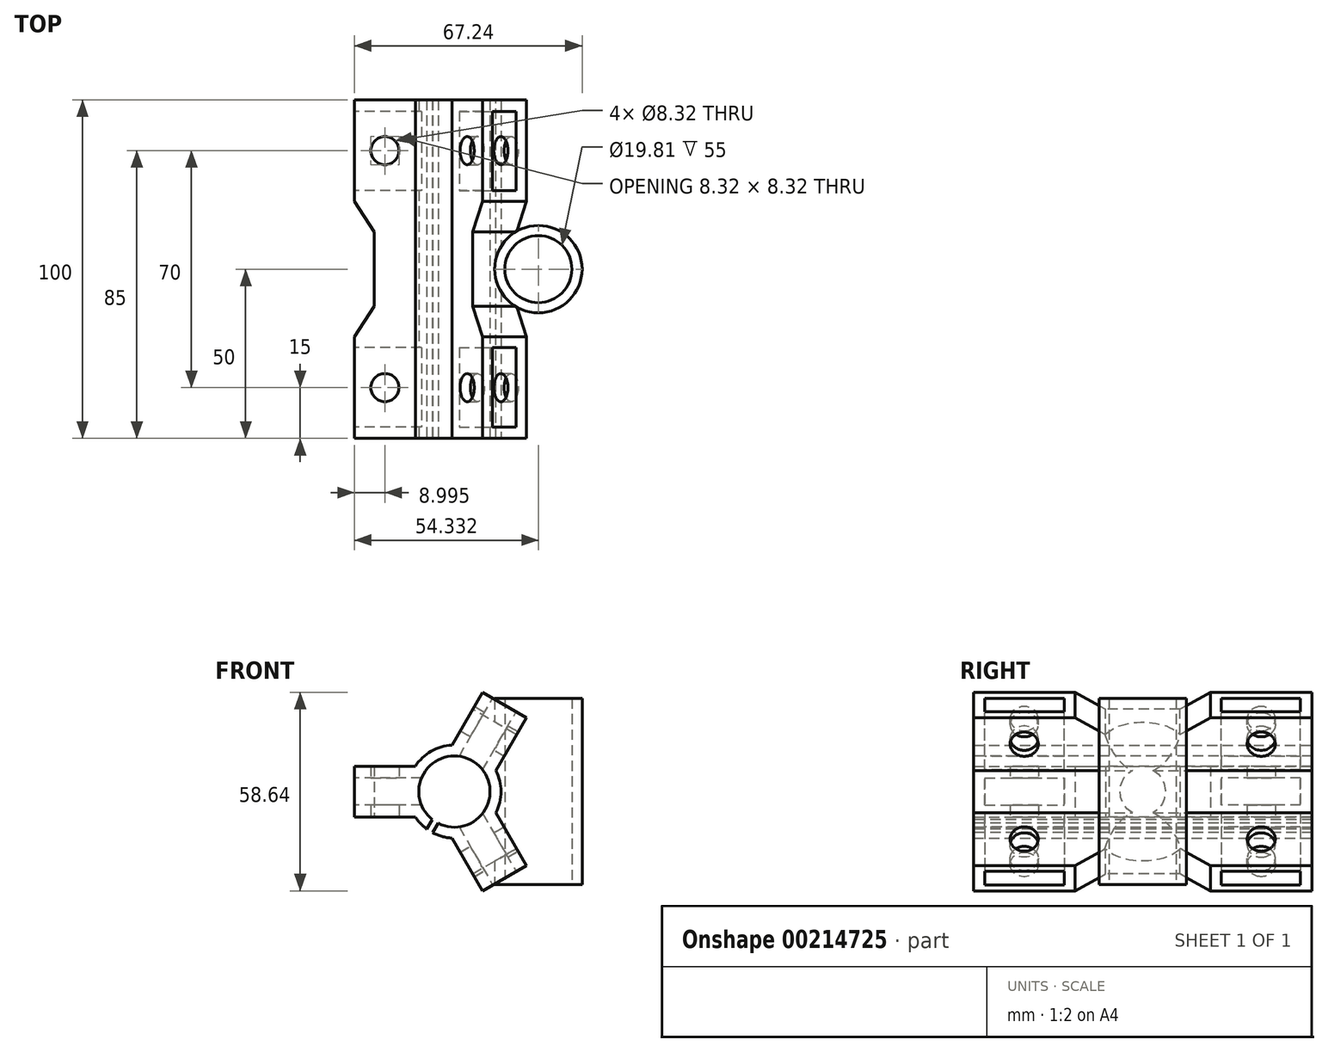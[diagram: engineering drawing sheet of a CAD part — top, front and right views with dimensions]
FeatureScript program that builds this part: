
annotation { "Feature Type Name" : "Feature", "Feature Type Description" : "" }
export const myFeature = defineFeature(function(context is Context, id is Id, definition is map)
    precondition{}
    {
        {
            var Q0;
            Q0=qCreatedBy(makeId("Top.planeOp"),FACE);
            var sketch = newSketch(context, id + "F0", { "sketchPlane" : qUnion([Q0])});
            skLineSegment(sketch, "E0", {"start": v(0, 0) * mm, "end": v(-9.53, 0) * mm, "construction": true});
            skLineSegment(sketch, "E1", {"start": v(-9.53, 0) * mm, "end": v(-9.53, 50) * mm, "construction": true});
            skLineSegment(sketch, "E2", {"start": v(-11.52, 0) * mm, "end": v(-11.53, 50) * mm});
            skLineSegment(sketch, "E3", {"start": v(-11.52, 0) * mm, "end": v(-29.52, 0) * mm});
            skLineSegment(sketch, "E4", {"start": v(-29.52, 0) * mm, "end": v(-29.53, 30) * mm});
            skCircle(sketch, "E5", {"center": v(-20.53, 15) * mm, "radius": 11 * mm, "construction": true});
            skCircle(sketch, "E6", {"center": v(-20.53, 15) * mm, "radius": 4.16 * mm});
            skLineSegment(sketch, "E7", {"start": v(-11.53, 39) * mm, "end": v(-23.75, 39) * mm, "construction": true});
            skLineSegment(sketch, "E8", {"start": v(-29.53, 30) * mm, "end": v(-23.75, 39) * mm});
            skLineSegment(sketch, "E9", {"start": v(-23.75, 39) * mm, "end": v(-23.75, 50) * mm});
            skLineSegment(sketch, "E10", {"start": v(-11.53, 50) * mm, "end": v(-23.75, 50) * mm, "construction": true});
            skLineSegment(sketch, "E11.MirrorCS", {"start": v(-23.75, 61) * mm, "end": v(-23.75, 50) * mm});
            skLineSegment(sketch, "E12.MirrorCS", {"start": v(-29.52, 70) * mm, "end": v(-23.75, 61) * mm});
            skLineSegment(sketch, "E13.MirrorCS", {"start": v(-29.53, 100) * mm, "end": v(-29.53, 70) * mm});
            skLineSegment(sketch, "E14.MirrorCS", {"start": v(-11.52, 100) * mm, "end": v(-29.52, 100) * mm});
            skLineSegment(sketch, "E15.MirrorCS", {"start": v(-11.53, 100) * mm, "end": v(-11.53, 50) * mm});
            skCircle(sketch, "E16.MirrorC", {"center": v(-20.53, 85) * mm, "radius": 4.16 * mm});
            skLineSegment(sketch, "E17.MirrorCS", {"start": v(-9.53, 100) * mm, "end": v(-9.53, 50) * mm, "construction": true});
            skCircle(sketch, "E18.MirrorC", {"center": v(-20.53, 85) * mm, "radius": 11 * mm, "construction": true});
            skSolve(sketch);
        }
        {
            var Q0;
            Q0=makeQuery(id+"F0.imprint","IMPRINT",FACE,{"disambiguationData":[TD([[makeQuery(id+"F0.imprint","IMPRINT",EDGE,{"derivedFrom":sQuery(id+"F0.wireOp",EDGE,"E2")}),1.0]])]});
            extrude(context, id + "F1", {"entities" : qUnion([Q0]), "depth" : 15 * mm});
        }
        {
            var Q0;
            Q0=makeQuery(id+"F1.opExtrude","SWEPT_FACE",FACE,{"disambiguationData":[OSD([sQuery(id+"F0.wireOp",EDGE,"E3")])]});
            var sketch = newSketch(context, id + "F2", { "sketchPlane" : qUnion([Q0])});
            skCircle(sketch, "E19", {"center": v(0, 7.5) * mm, "radius": 13.75 * mm, "construction": true});
            skCircle(sketch, "E20", {"center": v(0, 7.5) * mm, "radius": 10.53 * mm, "construction": true});
            skPoint(sketch, "E21.endSnap0", {"position": v(-11.52, 7.5) * mm});
            skArc(sketch, "E22", {"start": v(-6.88, 19.4) * mm, "mid": v(-13.75, 7.5) * mm, "end": v(-6.88, -4.4) * mm});
            skLineSegment(sketch, "E23", {"start": v(0, 7.5) * mm, "end": v(-10.53, 7.5) * mm, "construction": true});
            skLineSegment(sketch, "E24", {"start": v(0, 7.5) * mm, "end": v(-5.26, -1.61) * mm, "construction": true});
            skLineSegment(sketch, "E25", {"start": v(0, 7.5) * mm, "end": v(-5.26, 16.61) * mm, "construction": true});
            skArc(sketch, "E26", {"start": v(-5.26, 16.61) * mm, "mid": v(-10.53, 7.5) * mm, "end": v(-5.26, -1.61) * mm});
            skLineSegment(sketch, "E27", {"start": v(-5.26, 16.61) * mm, "end": v(-6.88, 19.4) * mm});
            skLineSegment(sketch, "E28", {"start": v(-5.26, -1.61) * mm, "end": v(-6.88, -4.4) * mm});
            skCircle(sketch, "E29", {"center": v(0, 7.5) * mm, "radius": 9.53 * mm, "construction": true});
            skSolve(sketch);
        }
        {
            var Q0;
            {var subQ0=sQuery(id+"F2.wireOp",EDGE,"E19");var subQ1=sQuery(id+"F0.wireOp",EDGE,"E3");var subQ2=makeQuery(id+"F1.opExtrude","SWEPT_EDGE",EDGE,{"disambiguationData":[OSD([sQuery(id+"F0.wireOp",EDGE,"E2"),subQ1])]});var subQ3=makeQuery(id+"F2.imprint","INTERSECT",VERTEX,{"derivedFrom":[subQ2,makeQuery(id+"F1.opExtrude","CAP_EDGE",EDGE,{"disambiguationData":[OSD([subQ1])],"isStart":true}),subQ0]});Q0=makeQuery(id+"F2.imprint","IMPRINT",FACE,{"disambiguationData":[TD([[makeQuery(id+"F2.imprint","IMPRINT",EDGE,{"disambiguationData":[TD([[subQ3,1.0]])],"derivedFrom":subQ0}),1.0]])]});}
            var Q1;
            {var subQ0=sQuery(id+"F2.wireOp",EDGE,"g3xJxAlq-R5pZ-Eeo2-CjEf-WmfwMOpCXLWw");Q1=makeQuery(id+"F2.imprint","IMPRINT",FACE,{"disambiguationData":[TD([[makeQuery(id+"F2.imprint","IMPRINT",EDGE,{"derivedFrom":subQ0}),-1.0]])]});}
            var Q2;
            Q2=makeQuery(id+"F2.imprint","IMPRINT",FACE,{"disambiguationData":[TD([[makeQuery(id+"F2.imprint","IMPRINT",EDGE,{"derivedFrom":sQuery(id+"F2.wireOp",EDGE,"E20")}),-1.0]])]});
            var Q3;
            Q3=makeQuery(id+"F2.imprint","IMPRINT",FACE,{"disambiguationData":[TD([[makeQuery(id+"F2.imprint","IMPRINT",EDGE,{"derivedFrom":sQuery(id+"F2.wireOp",EDGE,"E26")}),-1.0]])]});
            extrude(context, id + "F3", {"entities" : qUnion([Q0, Q1, Q2, Q3]), "operationType" : NewBodyOperationType.ADD, "oppositeDirection" : true, "offsetDistance" : 25 * mm, "depth" : 100 * mm});
        }
        {
            var Q0;
            Q0=makeQuery(id+"F1.opExtrude","SWEPT_FACE",FACE,{"disambiguationData":[OSD([sQuery(id+"F0.wireOp",EDGE,"E13.MirrorCS")])]});
            var sketch = newSketch(context, id + "F4", { "sketchPlane" : qUnion([Q0])});
            skLineSegment(sketch, "E30.bottom", {"start": v(-96.6, 11.5) * mm, "end": v(-73.2, 11.5) * mm});
            skLineSegment(sketch, "E30.top", {"start": v(-96.6, 3.5) * mm, "end": v(-73.2, 3.5) * mm});
            skLineSegment(sketch, "E30.left", {"start": v(-96.6, 11.5) * mm, "end": v(-96.6, 3.5) * mm});
            skLineSegment(sketch, "E30.right", {"start": v(-73.2, 11.5) * mm, "end": v(-73.2, 3.5) * mm});
            skLineSegment(sketch, "E31.bottom", {"start": v(-3.4, 3.5) * mm, "end": v(-26.8, 3.5) * mm});
            skLineSegment(sketch, "E31.top", {"start": v(-3.4, 11.5) * mm, "end": v(-26.8, 11.5) * mm});
            skLineSegment(sketch, "E31.left", {"start": v(-3.4, 3.5) * mm, "end": v(-3.4, 11.5) * mm});
            skLineSegment(sketch, "E31.right", {"start": v(-26.8, 3.5) * mm, "end": v(-26.8, 11.5) * mm});
            skSolve(sketch);
        }
        {
            var Q0;
            Q0=makeQuery(id+"F4.imprint","IMPRINT",FACE,{"disambiguationData":[TD([[makeQuery(id+"F4.imprint","IMPRINT",EDGE,{"derivedFrom":sQuery(id+"F4.wireOp",EDGE,"E30.bottom")}),-1.0]])]});
            var Q1;
            Q1=makeQuery(id+"F4.imprint","IMPRINT",FACE,{"disambiguationData":[TD([[makeQuery(id+"F4.imprint","IMPRINT",EDGE,{"derivedFrom":sQuery(id+"F4.wireOp",EDGE,"E31.bottom")}),-1.0]])]});
            extrude(context, id + "F5", {"entities" : qUnion([Q0, Q1]), "operationType" : NewBodyOperationType.REMOVE, "oppositeDirection" : true, "offsetDistance" : 25 * mm, "depth" : 25 * mm});
        }
        {
            var Q0;
            {var subQ0=sQuery(id+"F0.wireOp",EDGE,"E3");Q0=makeQuery(id+"F3.boolean.opBoolean","MERGE",FACE,{"derivedFrom":[makeQuery(id+"F1.opExtrude","SWEPT_FACE",FACE,{"disambiguationData":[OSD([subQ0])]}),makeQuery(id+"F3.opExtrude","CAP_FACE",FACE,{"disambiguationData":[OSD([sQuery(id+"F0.wireOp",EDGE,"E2"),subQ0,sQuery(id+"F2.wireOp",EDGE,"E22"),sQuery(id+"F2.wireOp",EDGE,"E26"),sQuery(id+"F2.wireOp",EDGE,"E27"),sQuery(id+"F2.wireOp",EDGE,"E28")])],"isStart":true})]});}
            var sketch = newSketch(context, id + "F6", { "sketchPlane" : qUnion([Q0])});
            skCircle(sketch, "E32", {"center": v(0, 7.5) * mm, "radius": 10.53 * mm});
            skSolve(sketch);
        }
        {
            var Q0;
            Q0=makeQuery(id+"F1.opExtrude","SWEPT_BODY",BODY,{"disambiguationData":[OSD([sQuery(id+"F0.wireOp",EDGE,"E2"),sQuery(id+"F0.wireOp",EDGE,"E3"),sQuery(id+"F0.wireOp",EDGE,"E4"),sQuery(id+"F0.wireOp",EDGE,"E6"),sQuery(id+"F0.wireOp",EDGE,"E8"),sQuery(id+"F0.wireOp",EDGE,"E9"),sQuery(id+"F0.wireOp",EDGE,"E11.MirrorCS"),sQuery(id+"F0.wireOp",EDGE,"E12.MirrorCS"),sQuery(id+"F0.wireOp",EDGE,"E13.MirrorCS"),sQuery(id+"F0.wireOp",EDGE,"E14.MirrorCS"),sQuery(id+"F0.wireOp",EDGE,"E15.MirrorCS"),sQuery(id+"F0.wireOp",EDGE,"E16.MirrorC")])]});
            var Q1;
            Q1=sQuery(id+"F6.wireOp",EDGE,"E32");
            circularPattern(context, id + "F7", {"operationType" : NewBodyOperationType.ADD, "entities" : qUnion([Q0]), "axis" : qUnion([Q1]), "angle" : 360 * degree, "instanceCount" : 3, "equalSpace" : true, "computeTransformsWithoutBuiltin" : true});
        }
        {
            var Q0;
            {var subQ0=sQuery(id+"F0.wireOp",EDGE,"E3");var subQ1=makeQuery(id+"F3.boolean.opBoolean","MERGE",FACE,{"derivedFrom":[makeQuery(id+"F1.opExtrude","SWEPT_FACE",FACE,{"disambiguationData":[OSD([subQ0])]}),makeQuery(id+"F3.opExtrude","CAP_FACE",FACE,{"disambiguationData":[OSD([sQuery(id+"F0.wireOp",EDGE,"E2"),subQ0,sQuery(id+"F2.wireOp",EDGE,"E22"),sQuery(id+"F2.wireOp",EDGE,"E26"),sQuery(id+"F2.wireOp",EDGE,"E27"),sQuery(id+"F2.wireOp",EDGE,"E28")])],"isStart":true})]});Q0=makeQuery(id+"F7.boolean.opBoolean","MERGE",FACE,{"derivedFrom":[subQ1,makeQuery(id+"F7.opPattern","COPY",FACE,{"derivedFrom":subQ1,"instanceName":"1"}),makeQuery(id+"F7.opPattern","COPY",FACE,{"derivedFrom":subQ1,"instanceName":"2"})]});}
            var sketch = newSketch(context, id + "F8", { "sketchPlane" : qUnion([Q0])});
            skLineSegment(sketch, "E33", {"start": v(-1.17, -5.98) * mm, "end": v(-11.96, 0.25) * mm, "construction": true});
            skLineSegment(sketch, "E34", {"start": v(-6.56, -2.87) * mm, "end": v(-8.22, -5.74) * mm, "construction": true});
            skLineSegment(sketch, "E35", {"start": v(-8.22, -5.74) * mm, "end": v(-7.36, -6.24) * mm});
            skLineSegment(sketch, "E36", {"start": v(-8.22, -5.74) * mm, "end": v(-9.09, -5.24) * mm});
            skLineSegment(sketch, "E37", {"start": v(-9.09, -5.24) * mm, "end": v(-6.5, -0.77) * mm});
            skLineSegment(sketch, "E38", {"start": v(-7.36, -6.24) * mm, "end": v(-4.78, -1.77) * mm});
            skLineSegment(sketch, "E39", {"start": v(-6.5, -0.77) * mm, "end": v(-4.78, -1.77) * mm});
            skSolve(sketch);
        }
        {
            var Q0;
            {var subQ0=sQuery(id+"F8.wireOp",EDGE,"E39");var subQ1=sQuery(id+"F8.wireOp",EDGE,"E37");var subQ2=makeQuery(id+"F3.opExtrude","CAP_EDGE",EDGE,{"disambiguationData":[OSD([sQuery(id+"F2.wireOp",EDGE,"E26")])],"isStart":true});var subQ3=makeQuery(id+"F7.boolean.opBoolean","MERGE",EDGE,{"derivedFrom":[subQ2,makeQuery(id+"F7.opPattern","COPY",EDGE,{"derivedFrom":subQ2,"instanceName":"1"}),makeQuery(id+"F7.opPattern","COPY",EDGE,{"derivedFrom":subQ2,"instanceName":"2"})]});var subQ4=makeQuery(id+"F8.imprint","INTERSECT",VERTEX,{"derivedFrom":[subQ3,subQ1,subQ0]});Q0=makeQuery(id+"F8.imprint","IMPRINT",FACE,{"disambiguationData":[TD([[makeQuery(id+"F8.imprint","IMPRINT",EDGE,{"disambiguationData":[TD([[subQ4,1.0]])],"derivedFrom":subQ1}),-1.0]])]});}
            var Q1;
            Q1 = qSketchRegion(id + "F10", true);
            extrude(context, id + "F9", {"entities" : qUnion([Q0, Q1]), "operationType" : NewBodyOperationType.REMOVE, "oppositeDirection" : true, "offsetDistance" : 25 * mm, "depth" : 130 * mm});
        }
        {
            var Q0;
            {var subQ0=sQuery(id+"F0.wireOp",EDGE,"E3");var subQ1=makeQuery(id+"F3.boolean.opBoolean","MERGE",FACE,{"derivedFrom":[makeQuery(id+"F1.opExtrude","SWEPT_FACE",FACE,{"disambiguationData":[OSD([subQ0])]}),makeQuery(id+"F3.opExtrude","CAP_FACE",FACE,{"disambiguationData":[OSD([sQuery(id+"F0.wireOp",EDGE,"E2"),subQ0,sQuery(id+"F2.wireOp",EDGE,"E22"),sQuery(id+"F2.wireOp",EDGE,"E26"),sQuery(id+"F2.wireOp",EDGE,"E27"),sQuery(id+"F2.wireOp",EDGE,"E28")])],"isStart":true})]});Q0=makeQuery(id+"F7.boolean.opBoolean","MERGE",FACE,{"derivedFrom":[subQ1,makeQuery(id+"F7.opPattern","COPY",FACE,{"derivedFrom":subQ1,"instanceName":"1"}),makeQuery(id+"F7.opPattern","COPY",FACE,{"derivedFrom":subQ1,"instanceName":"2"})]});}
            var sketch = newSketch(context, id + "F10", { "sketchPlane" : qUnion([Q0])});
            skCircle(sketch, "E40", {"center": v(0, 7.5) * mm, "radius": 10.53 * mm});
            skSolve(sketch);
        }
        {
            var Q0;
            {var subQ0=sQuery(id+"F10.wireOp",EDGE,"E40");var subQ1=makeQuery(id+"F10.imprint","INTERSECT",VERTEX,{"derivedFrom":[makeQuery(id+"F9.boolean.opBoolean","COPY",EDGE,{"derivedFrom":makeQuery(id+"F9.opExtrude","CAP_EDGE",EDGE,{"disambiguationData":[OSD([sQuery(id+"F8.wireOp",EDGE,"E37")])],"isStart":true})}),subQ0]});Q0=makeQuery(id+"F10.imprint","IMPRINT",FACE,{"disambiguationData":[TD([[makeQuery(id+"F10.imprint","IMPRINT",EDGE,{"disambiguationData":[TD([[subQ1,1.0]])],"derivedFrom":subQ0}),1.0]])]});}
            extrude(context, id + "F11", {"entities" : qUnion([Q0]), "operationType" : NewBodyOperationType.REMOVE, "oppositeDirection" : true, "depth" : 100 * mm});
        }
        {
            var Q0;
            Q0=qCreatedBy(makeId("Top.planeOp"),FACE);
            var sketch = newSketch(context, id + "F12", { "sketchPlane" : qUnion([Q0])});
            skCircle(sketch, "E41", {"center": v(24.81, 50) * mm, "radius": 9.9 * mm});
            skCircle(sketch, "E42", {"center": v(24.81, 50) * mm, "radius": 12.9 * mm});
            skSolve(sketch);
        }
        {
            var Q0;
            Q0=makeQuery(id+"F12.imprint","IMPRINT",FACE,{"disambiguationData":[TD([[makeQuery(id+"F12.imprint","IMPRINT",EDGE,{"derivedFrom":sQuery(id+"F12.wireOp",EDGE,"E41")}),-1.0]])]});
            extrude(context, id + "F13", {"entities" : qUnion([Q0]), "operationType" : NewBodyOperationType.ADD, "depth" : 35 * mm, "hasSecondDirection" : true, "secondDirectionOppositeDirection" : true, "secondDirectionDepth" : 20 * mm});
        }
        {
            var Q0;
            Q0=makeQuery(id+"F13.opExtrude","CAP_FACE",FACE,{"disambiguationData":[OSD([sQuery(id+"F12.wireOp",EDGE,"E41"),sQuery(id+"F12.wireOp",EDGE,"E42")])],"isStart":true});
            var sketch = newSketch(context, id + "F14", { "sketchPlane" : qUnion([Q0])});
            skCircle(sketch, "E43", {"center": v(24.81, -50) * mm, "radius": 9.9 * mm});
            skSolve(sketch);
        }
        {
            var Q0;
            Q0=makeQuery(id+"F14.imprint","IMPRINT",FACE,{"disambiguationData":[TD([[makeQuery(id+"F14.imprint","IMPRINT",EDGE,{"derivedFrom":sQuery(id+"F14.wireOp",EDGE,"E43")}),-1.0]])]});
            extrude(context, id + "F15", {"entities" : qUnion([Q0]), "operationType" : NewBodyOperationType.REMOVE, "oppositeDirection" : true, "depth" : 60 * mm});
        }
    });
